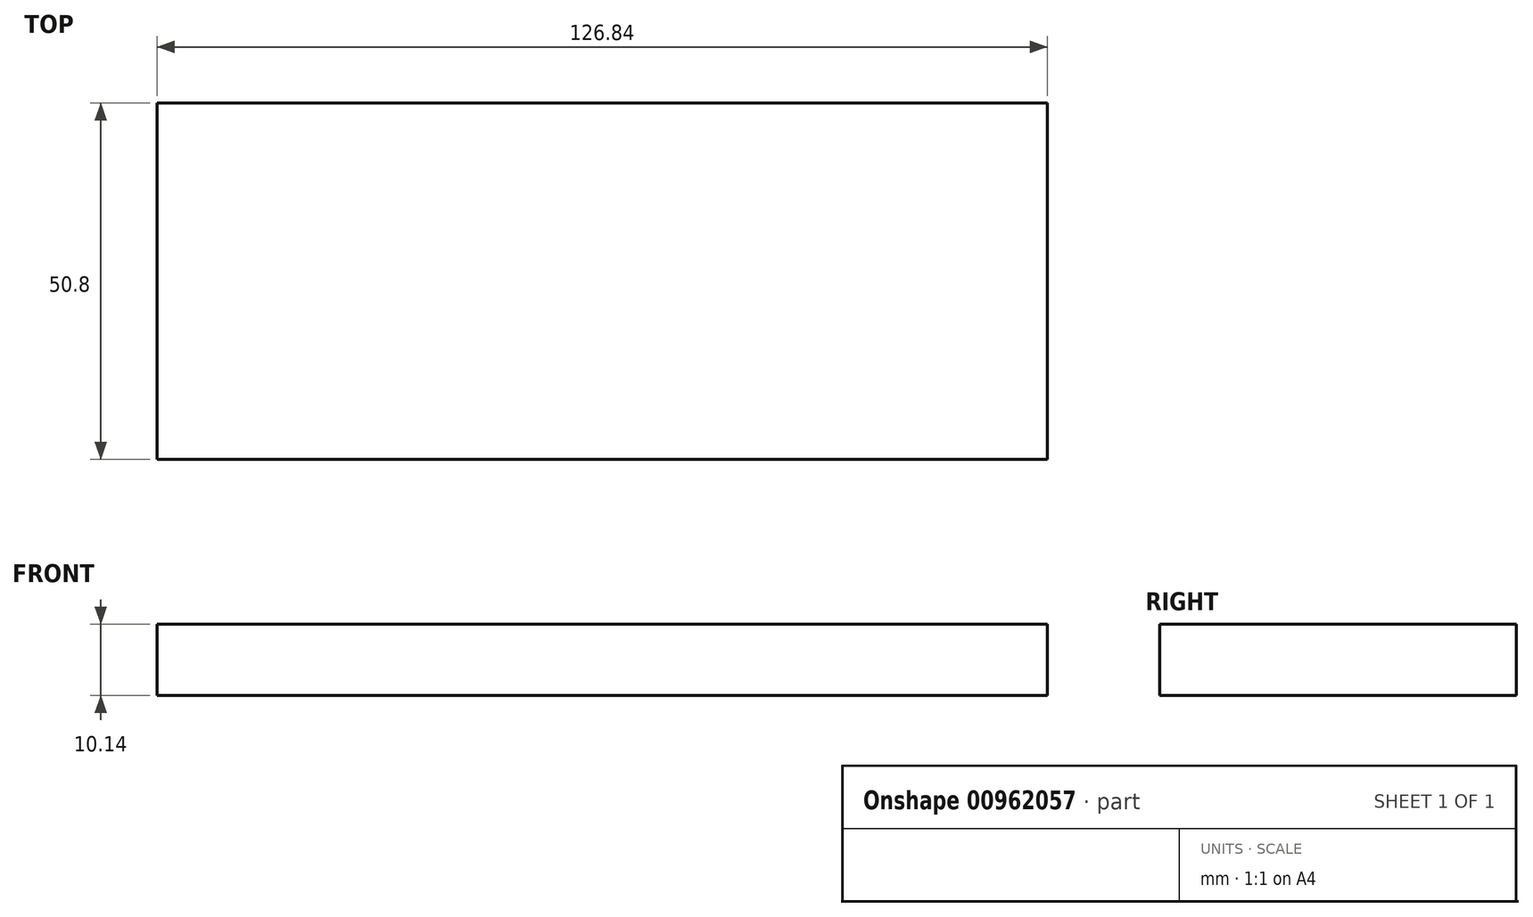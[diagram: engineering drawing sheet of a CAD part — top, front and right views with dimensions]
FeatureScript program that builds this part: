
annotation { "Feature Type Name" : "Feature", "Feature Type Description" : "" }
export const myFeature = defineFeature(function(context is Context, id is Id, definition is map)
    precondition{}
    {
        {
            var Q0;
            Q0=qCreatedBy(makeId("Front.planeOp"),FACE);
            var sketch = newSketch(context, id + "F0", { "sketchPlane" : qUnion([Q0])});
            skLineSegment(sketch, "E0.bottom", {"start": v(-66.28, 51.16) * mm, "end": v(60.56, 51.16) * mm});
            skLineSegment(sketch, "E0.top", {"start": v(-66.28, 41.02) * mm, "end": v(60.56, 41.02) * mm});
            skLineSegment(sketch, "E0.left", {"start": v(-66.28, 51.16) * mm, "end": v(-66.28, 41.02) * mm});
            skLineSegment(sketch, "E0.right", {"start": v(60.56, 51.16) * mm, "end": v(60.56, 41.02) * mm});
            skSolve(sketch);
        }
        {
            var Q0;
            Q0=makeQuery(id+"F0.imprint","IMPRINT",FACE,{"disambiguationData":[TD([[makeQuery(id+"F0.imprint","IMPRINT",EDGE,{"derivedFrom":sQuery(id+"F0.wireOp",EDGE,"E0.bottom")}),-1.0]])]});
            extrude(context, id + "F1", {"entities" : qUnion([Q0]), "depth" : 50.8 * mm, "offsetDistance" : 25.4 * mm});
        }
    });
